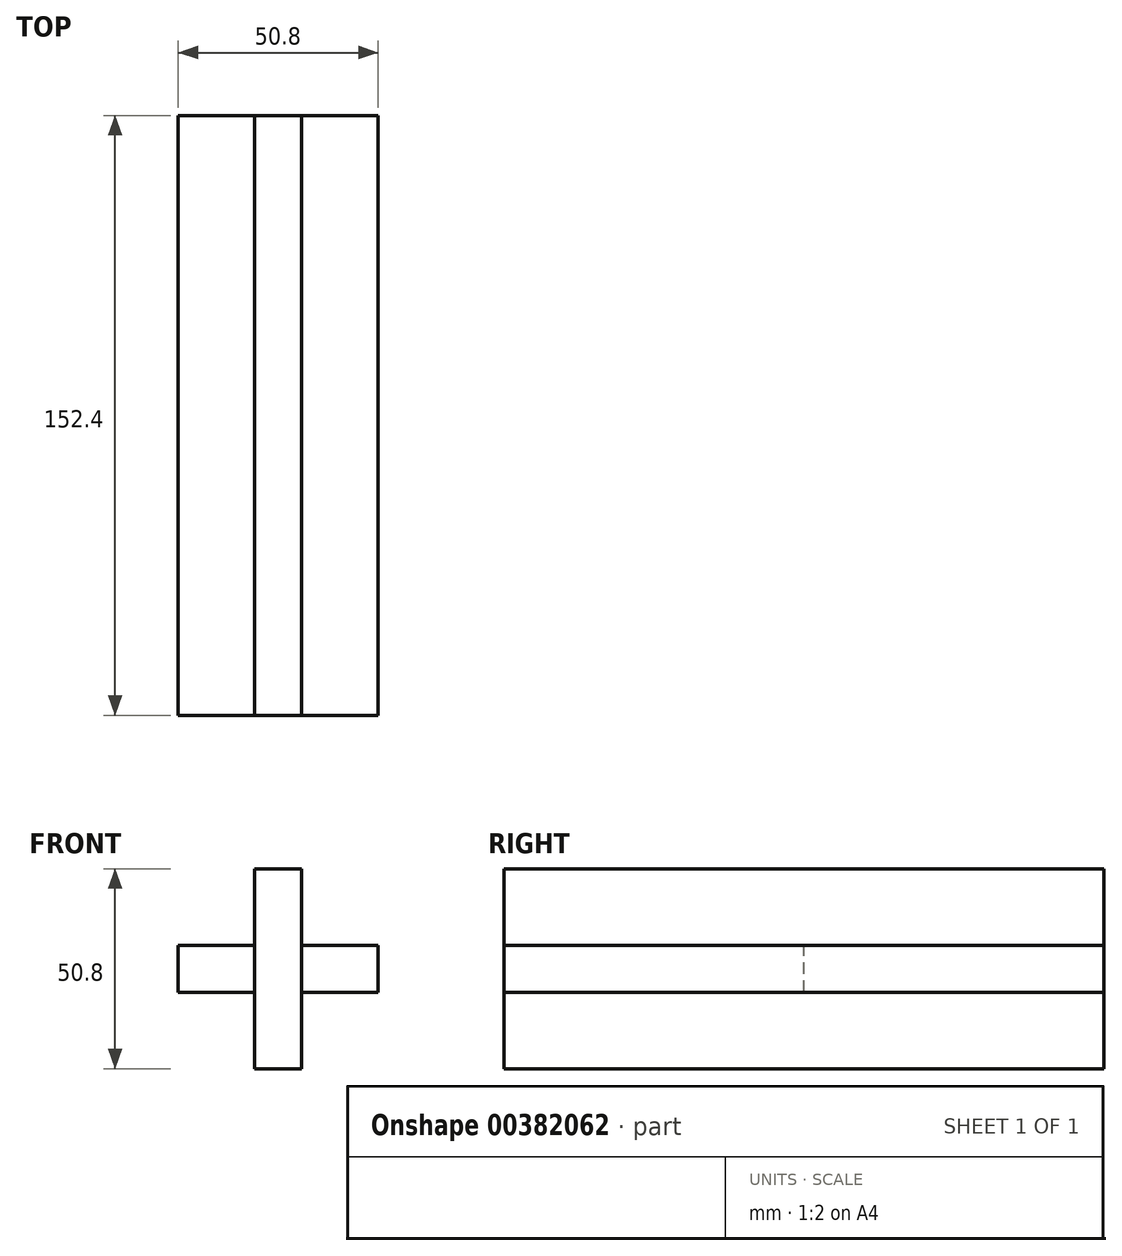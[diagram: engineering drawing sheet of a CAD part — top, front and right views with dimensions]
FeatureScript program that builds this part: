
annotation { "Feature Type Name" : "Feature", "Feature Type Description" : "" }
export const myFeature = defineFeature(function(context is Context, id is Id, definition is map)
    precondition{}
    {
        {
            var Q0;
            Q0=qCreatedBy(makeId("Top.planeOp"),FACE);
            var sketch = newSketch(context, id + "F0", { "sketchPlane" : qUnion([Q0])});
            skLineSegment(sketch, "E0.bottom", {"start": v(-23.42, 0) * mm, "end": v(-4, 0) * mm});
            skLineSegment(sketch, "E0.top", {"start": v(-23.42, 152.4) * mm, "end": v(27.38, 152.4) * mm});
            skLineSegment(sketch, "E0.left", {"start": v(-23.42, 0) * mm, "end": v(-23.42, 152.4) * mm});
            skLineSegment(sketch, "E0.right", {"start": v(27.38, 0) * mm, "end": v(27.38, 152.4) * mm});
            skLineSegment(sketch, "E1", {"start": v(-4, 0) * mm, "end": v(-4, 76.2) * mm});
            skLineSegment(sketch, "E2", {"start": v(-4, 76.2) * mm, "end": v(7.96, 76.2) * mm});
            skLineSegment(sketch, "E3", {"start": v(7.96, 76.2) * mm, "end": v(7.96, 0) * mm});
            skLineSegment(sketch, "E4.trimOffspring", {"start": v(7.96, 0) * mm, "end": v(27.38, 0) * mm});
            skSolve(sketch);
        }
        {
            var Q0;
            Q0=makeQuery(id+"F0.imprint","IMPRINT",FACE,{"disambiguationData":[TD([[makeQuery(id+"F0.imprint","IMPRINT",EDGE,{"derivedFrom":sQuery(id+"F0.wireOp",EDGE,"E0.bottom")}),1.0]])]});
            extrude(context, id + "F1", {"entities" : qUnion([Q0]), "depth" : 11.94 * mm});
        }
        {
            var Q0;
            Q0=makeQuery(id+"F1.opExtrude","SWEPT_FACE",FACE,{"disambiguationData":[OSD([sQuery(id+"F0.wireOp",EDGE,"E0.top")])]});
            var sketch = newSketch(context, id + "F2", { "sketchPlane" : qUnion([Q0])});
            skLineSegment(sketch, "E5", {"start": v(-7.95, 11.94) * mm, "end": v(-7.95, 31.37) * mm});
            skLineSegment(sketch, "E6", {"start": v(4, 11.94) * mm, "end": v(4, 31.37) * mm});
            skLineSegment(sketch, "E7", {"start": v(4, 31.37) * mm, "end": v(-7.95, 31.37) * mm});
            skLineSegment(sketch, "E8.MirrorCS", {"start": v(4, 0) * mm, "end": v(4, -19.43) * mm});
            skLineSegment(sketch, "E9.MirrorCS", {"start": v(-7.95, 0) * mm, "end": v(-7.95, -19.43) * mm});
            skLineSegment(sketch, "E10.MirrorCS", {"start": v(4, -19.43) * mm, "end": v(-7.95, -19.43) * mm});
            skSolve(sketch);
        }
        {
            var Q0;
            {var subQ0=sQuery(id+"F2.wireOp",EDGE,"E5");Q0=makeQuery(id+"F2.imprint","IMPRINT",FACE,{"disambiguationData":[TD([[makeQuery(id+"F2.imprint","IMPRINT",EDGE,{"derivedFrom":subQ0}),-1.0]])]});}
            var Q1;
            {var subQ0=sQuery(id+"F2.wireOp",EDGE,"E8.MirrorCS");Q1=makeQuery(id+"F2.imprint","IMPRINT",FACE,{"disambiguationData":[TD([[makeQuery(id+"F2.imprint","IMPRINT",EDGE,{"derivedFrom":subQ0}),-1.0]])]});}
            extrude(context, id + "F3", {"entities" : qUnion([Q0, Q1]), "operationType" : NewBodyOperationType.ADD, "oppositeDirection" : true, "depth" : 152.4 * mm});
        }
        {
            var Q0;
            {var subQ0=sQuery(id+"F0.wireOp",EDGE,"E0.top");var subQ1=makeQuery(id+"F1.opExtrude","CAP_EDGE",EDGE,{"disambiguationData":[OSD([subQ0])],"isStart":false});Q0=makeQuery(id+"F3.opExtrude","SWEPT_FACE",FACE,{"disambiguationData":[OSD([subQ0]),TDD([makeQuery(id+"F2.imprint","IMPRINT",EDGE,{"disambiguationData":[TD([[makeQuery(id+"F2.imprint","INTERSECT",VERTEX,{"derivedFrom":[subQ1,sQuery(id+"F2.wireOp",EDGE,"E5")]}),1.0]])],"derivedFrom":subQ1})])]});}
            var sketch = newSketch(context, id + "F4", { "sketchPlane" : qUnion([Q0])});
            skLineSegment(sketch, "E11", {"start": v(-4, -76.2) * mm, "end": v(7.95, -76.2) * mm});
            skLineSegment(sketch, "E12", {"start": v(7.95, -76.2) * mm, "end": v(7.95, 0) * mm});
            skLineSegment(sketch, "E13", {"start": v(7.95, 0) * mm, "end": v(-4, 0) * mm});
            skLineSegment(sketch, "E14", {"start": v(-4, 0) * mm, "end": v(-4, -76.2) * mm});
            skSolve(sketch);
        }
        {
            var Q0;
            Q0=makeQuery(id+"F4.imprint","IMPRINT",FACE,{"disambiguationData":[TD([[makeQuery(id+"F4.imprint","IMPRINT",EDGE,{"derivedFrom":sQuery(id+"F4.wireOp",EDGE,"E11")}),1.0]])]});
            extrude(context, id + "F5", {"entities" : qUnion([Q0]), "operationType" : NewBodyOperationType.ADD, "depth" : 11.94 * mm});
        }
    });
